# Revit family: TESK_Насос вертикальный с овальными фланцами_SVMT-20
name_source: partatom
category: Оборудование
units: mm (PartAtom-declared; Revit-internal decimal feet)

## family parameters
Всегда вертикально = Да
Классификация = Насос
На основе рабочей плоскости = Нет
Общий = Нет
При загрузке вырезать с полостями = Нет
Размер круглого соединителя = Использовать диаметр
Тип детали = Вставляется
Точка расчета площади = Нет

## types (12) — shared parameters
ADSK_Версия Revit = 2019
ADSK_Версия семейства = 1.0
ADSK_Диаметр условный = 50 мм
ADSK_Единица измерения = шт.
ADSK_Завод-изготовитель = TESK
ADSK_Классификация нагрузок = Прочее
ADSK_Количество = 1
ADSK_Количество фаз = 3
ADSK_Количество фаз числовое = 3
ADSK_Коэффициент мощности = 1
ADSK_Наименование краткое = Вертикальный многоступенчатый центробежный насос
ADSK_Напряжение = 400 В
URL = www.teskpump.ru
Длина_ВспомЛиния = 30 мм
Материал_1 = TESK_Черный_Условный
Материал_2 = TESK_Нержавеющая сталь
Материал_КорпусДвигателя = TESK_Черный_Ребра_Условный
Материал_КорпусУлитка = TESK_Черный_Условный
Таблица_Поиска = TESK_SVMT-20 ОФ
УГО_Длина = 250 мм
Фланец_Толщина = 25 мм

## per-type parameters (varying)
| type | ADSK_Код изделия | ADSK_Масса | ADSK_Масса_Текст | ADSK_Наименование | ADSK_Номинальная мощность | ADSK_Полная мощность | Высота_Корпуса | Высота_Перехода | Двигатель_Высота | Двигатель_ОтступКоробки | Двигатель_Ширина | Напор максимальный |
| SVMT 20-1 1.1kW 3x380V 50Hz IE3 | 7720-10003380NF | 33 | 33 | Вертикальный многоступенчатый центробежный насос SVMT, DN50, Hmax=13.5м (3x380V 50Hz IE3) | 1 кВт | 1 кВ·А | 387 мм | 130 мм | 280 мм | 142 мм | 170 мм | 13.5 |
| SVMT 20-2 2.2kW 3x380V 50Hz IE3 | 7720-20003380NF | 42 | 42 | Вертикальный многоступенчатый центробежный насос SVMT, DN50, Hmax=27м (3x380V 50Hz IE3) | 2 кВт | 2 кВ·А | 397 мм | 150 мм | 333 мм | 155 мм | 190 мм | 27 |
| SVMT 20-3 4kW 3x380V 50Hz IE3 | 7720-30003380NF | 58 | 58 | Вертикальный многоступенчатый центробежный насос SVMT, DN50, Hmax=40м (3x380V 50Hz IE3) | 4 кВт | 4 кВ·А | 452 мм | 170 мм | 382 мм | 188 мм | 230 мм | 40 |
| SVMT 20-4 5.5kW 3x380V 50Hz IE3 | 7720-40003380NF | 74 | 74 | Вертикальный многоступенчатый центробежный насос SVMT, DN50, Hmax=54м (3x380V 50Hz IE3) | 6 кВт | 6 кВ·А | 517 мм | 210 мм | 435 мм | 208 мм | 260 мм | 54 |
| SVMT 20-5 5.5kW 3x380V 50Hz IE3 | 7720-50003380NF | 76 | 76 | Вертикальный многоступенчатый центробежный насос SVMT, DN50, Hmax=67м (3x380V 50Hz IE3) | 6 кВт | 6 кВ·А | 562 мм | 210 мм | 435 мм | 208 мм | 260 мм | 67 |
| SVMT 20-6 7.5kW 3x380V 50Hz IE3 | 7720-60003380NF | 82 | 82 | Вертикальный многоступенчатый центробежный насос SVMT, DN50, Hmax=81м (3x380V 50Hz IE3) | 8 кВт | 8 кВ·А | 607 мм | 210 мм | 435 мм | 208 мм | 260 мм | 81 |
| SVMT 20-7 7.5kW 3x380V 50Hz IE3 | 7720-70003380NF | 84 | 84 | Вертикальный многоступенчатый центробежный насос SVMT, DN50, Hmax=95м (3x380V 50Hz IE3) | 8 кВт | 8 кВ·А | 652 мм | 210 мм | 435 мм | 208 мм | 260 мм | 95 |
| SVMT 20-8 11kW 3x380V 50Hz IE3 | 7720-80003380NF | 153 | 153 | Вертикальный многоступенчатый центробежный насос SVMT, DN50, Hmax=109м (3x380V 50Hz IE3) | 11 кВт | 11 кВ·А | 697 мм | 230 мм | 580 мм | 260 мм | 350 мм | 109 |
| SVMT 20-10 11kW 3x380V 50Hz IE3 | 7720-100003380NF | 157 | 157 | Вертикальный многоступенчатый центробежный насос SVMT, DN50, Hmax=136м (3x380V 50Hz IE3) | 11 кВт | 11 кВ·А | 875 мм | 230 мм | 580 мм | 260 мм | 350 мм | 136 |
| SVMT 20-12 15kW 3x380V 50Hz IE3 | 7720-120003380NF | 170 | 170 | Вертикальный многоступенчатый центробежный насос SVMT, DN50, Hmax=164м (3x380V 50Hz IE3) | 15 кВт | 15 кВ·А | 965 мм | 230 мм | 580 мм | 260 мм | 350 мм | 164 |
| SVMT 20-14 15kW 3x380V 50Hz IE3 | 7720-140003380NF | 172 | 172 | Вертикальный многоступенчатый центробежный насос SVMT, DN50, Hmax=192м (3x380V 50Hz IE3) | 15 кВт | 15 кВ·А | 1055 мм | 230 мм | 580 мм | 260 мм | 350 мм | 192 |
| SVMT 20-17 18.5kW 3x380V 50Hz IE3 | 7720-170003380NF | 195 | 195 | Вертикальный многоступенчатый центробежный насос SVMT, DN50, Hmax=234м (3x380V 50Hz IE3) | 19 кВт | 19 кВ·А | 1190 мм | 250 мм | 610 мм | 260 мм | 350 мм | 234 |

note: column(s) folded — value = type name in every type: ADSK_Марка
